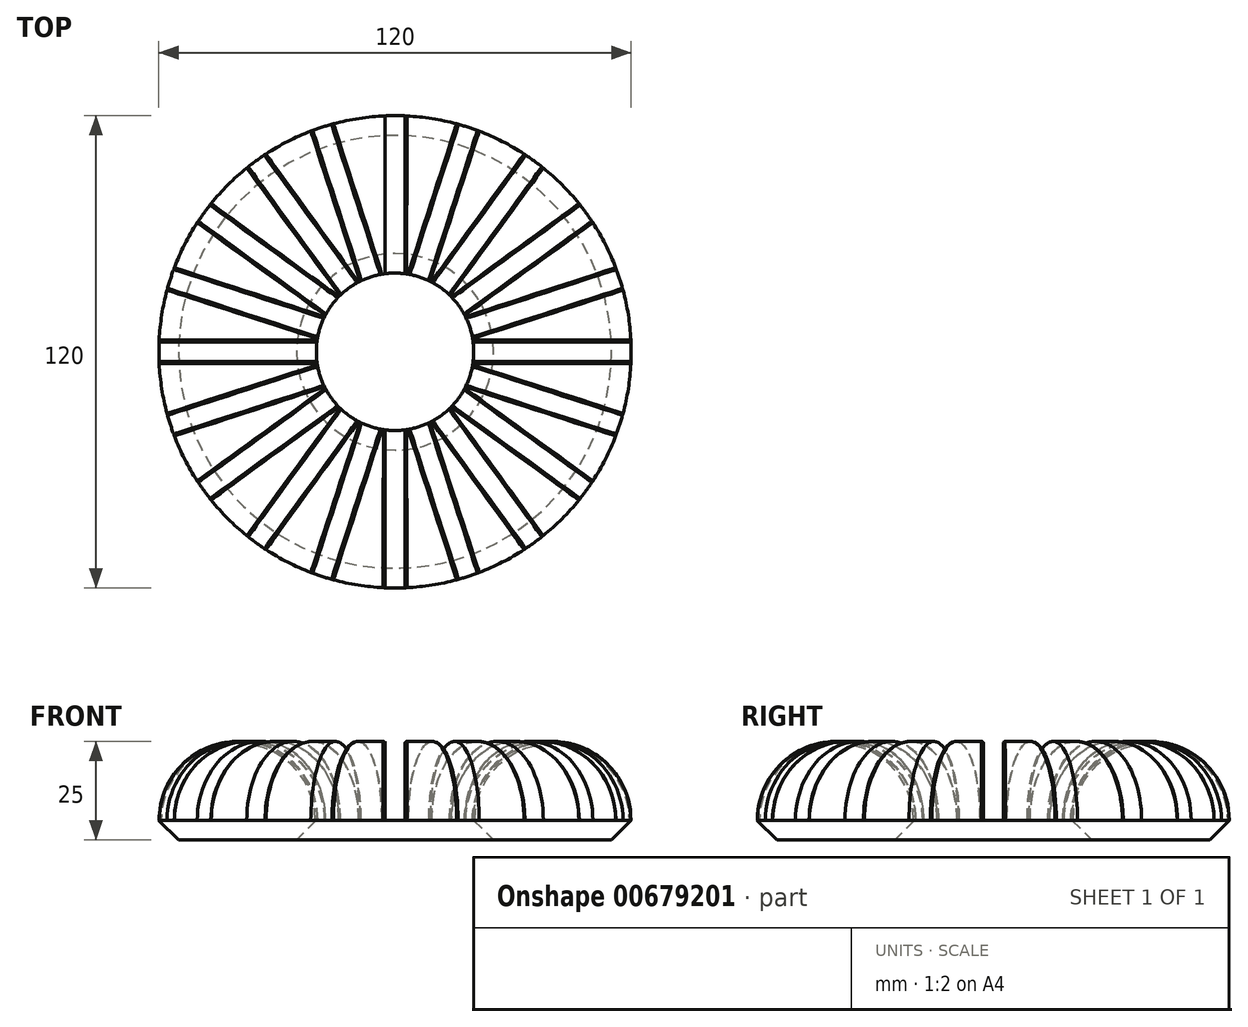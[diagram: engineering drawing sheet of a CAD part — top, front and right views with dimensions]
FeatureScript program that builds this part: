
annotation { "Feature Type Name" : "Feature", "Feature Type Description" : "" }
export const myFeature = defineFeature(function(context is Context, id is Id, definition is map)
    precondition{}
    {
        {
            var Q0;
            Q0=qCreatedBy(makeId("Front.planeOp"),FACE);
            var sketch = newSketch(context, id + "F0", { "sketchPlane" : qUnion([Q0])});
            skCircle(sketch, "E0", {"center": v(-40, 0) * mm, "radius": 20 * mm});
            skLineSegment(sketch, "E1", {"start": v(0, 10.53) * mm, "end": v(0, -11.09) * mm, "construction": true});
            skSolve(sketch);
        }
        {
            var Q0;
            Q0=makeQuery(id+"F0.imprint","IMPRINT",FACE,{"disambiguationData":[TD([[makeQuery(id+"F0.imprint","IMPRINT",EDGE,{"derivedFrom":sQuery(id+"F0.wireOp",EDGE,"E0")}),1.0]])]});
            var Q1;
            Q1=sQuery(id+"F0.wireOp",EDGE,"E1");
            revolve(context, id + "F1", {"entities" : qUnion([Q0]), "axis" : qUnion([Q1]), "revolveType" : RevolveType.FULL});
        }
        {
            var Q0;
            Q0=qCreatedBy(makeId("Top.planeOp"),FACE);
            var sketch = newSketch(context, id + "F2", { "sketchPlane" : qUnion([Q0])});
            skLineSegment(sketch, "E2.bottom", {"start": v(-120, 2.5) * mm, "end": v(0, 2.5) * mm});
            skLineSegment(sketch, "E2.top", {"start": v(-120, -2.5) * mm, "end": v(0, -2.5) * mm});
            skLineSegment(sketch, "E2.left", {"start": v(-120, 2.5) * mm, "end": v(-120, -2.5) * mm});
            skLineSegment(sketch, "E2.right", {"start": v(0, 2.5) * mm, "end": v(0, -2.5) * mm});
            skSolve(sketch);
        }
        {
            var Q0;
            Q0=makeQuery(id+"F2.imprint","IMPRINT",FACE,{"disambiguationData":[TD([[makeQuery(id+"F2.imprint","IMPRINT",EDGE,{"derivedFrom":sQuery(id+"F2.wireOp",EDGE,"E2.bottom")}),-1.0]])]});
            extrude(context, id + "F3", {"entities" : qUnion([Q0]), "depth" : 25 * mm, "offsetDistance" : 25 * mm});
        }
        {
            var Q0;
            Q0=makeQuery(id+"F3.opExtrude","SWEPT_BODY",BODY,{"disambiguationData":[OSD([sQuery(id+"F2.wireOp",EDGE,"E2.bottom"),sQuery(id+"F2.wireOp",EDGE,"E2.top"),sQuery(id+"F2.wireOp",EDGE,"E2.left"),sQuery(id+"F2.wireOp",EDGE,"E2.right")])]});
            var Q1;
            Q1=makeQuery(id+"F1.opRevolve","SWEPT_FACE",FACE,{"disambiguationData":[OSD([sQuery(id+"F0.wireOp",EDGE,"E0")])]});
            circularPattern(context, id + "F4", {"operationType" : NewBodyOperationType.REMOVE, "entities" : qUnion([Q0]), "axis" : qUnion([Q1]), "angle" : 360 * degree, "instanceCount" : 20, "equalSpace" : true});
        }
        {
            var Q0;
            Q0=qCreatedBy(makeId("Right.planeOp"),FACE);
            var sketch = newSketch(context, id + "F5", { "sketchPlane" : qUnion([Q0])});
            skLineSegment(sketch, "E3.bottom", {"start": v(-64.64, -5) * mm, "end": v(73.85, -5) * mm});
            skLineSegment(sketch, "E3.top", {"start": v(-64.64, -32.55) * mm, "end": v(73.85, -32.55) * mm});
            skLineSegment(sketch, "E3.left", {"start": v(-64.64, -5) * mm, "end": v(-64.64, -32.55) * mm});
            skLineSegment(sketch, "E3.right", {"start": v(73.85, -5) * mm, "end": v(73.85, -32.55) * mm});
            skSolve(sketch);
        }
        {
            var Q0;
            Q0=makeQuery(id+"F5.imprint","IMPRINT",FACE,{"disambiguationData":[TD([[makeQuery(id+"F5.imprint","IMPRINT",EDGE,{"derivedFrom":sQuery(id+"F5.wireOp",EDGE,"E3.bottom")}),-1.0]])]});
            extrude(context, id + "F6", {"entities" : qUnion([Q0]), "operationType" : NewBodyOperationType.REMOVE, "endBound" : BoundingType.SYMMETRIC, "oppositeDirection" : true, "depth" : 180 * mm, "offsetDistance" : 25 * mm});
        }
        {
            var Q0;
            Q0=makeQuery(id+"F6.boolean.opBoolean","INTERSECT",EDGE,{"disambiguationData":[OD(0.0)],"derivedFrom":[makeQuery(id+"F1.opRevolve","SWEPT_FACE",FACE,{"disambiguationData":[OSD([sQuery(id+"F0.wireOp",EDGE,"E0")])]}),makeQuery(id+"F6.opExtrude","SWEPT_FACE",FACE,{"disambiguationData":[OSD([sQuery(id+"F5.wireOp",EDGE,"E3.bottom")])]})]});
            var Q1;
            Q1=makeQuery(id+"F6.boolean.opBoolean","INTERSECT",EDGE,{"disambiguationData":[OD(1.0)],"derivedFrom":[makeQuery(id+"F1.opRevolve","SWEPT_FACE",FACE,{"disambiguationData":[OSD([sQuery(id+"F0.wireOp",EDGE,"E0")])]}),makeQuery(id+"F6.opExtrude","SWEPT_FACE",FACE,{"disambiguationData":[OSD([sQuery(id+"F5.wireOp",EDGE,"E3.bottom")])]})]});
            chamfer(context, id + "F7", {"entities" : qUnion([Q0, Q1]), "width" : 5 * mm, "tangentPropagation" : true});
        }
        {
            var Q0;
            Q0=makeQuery(id+"F4.boolean.opBoolean","INTERSECT",EDGE,{"derivedFrom":[makeQuery(id+"F1.opRevolve","SWEPT_FACE",FACE,{"disambiguationData":[OSD([sQuery(id+"F0.wireOp",EDGE,"E0")])]}),makeQuery(id+"F4.opPattern","COPY",FACE,{"derivedFrom":makeQuery(id+"F3.opExtrude","SWEPT_FACE",FACE,{"disambiguationData":[OSD([sQuery(id+"F2.wireOp",EDGE,"E2.bottom")])]}),"instanceName":"4"})]});
            var Q1;
            Q1=makeQuery(id+"F4.boolean.opBoolean","INTERSECT",EDGE,{"derivedFrom":[makeQuery(id+"F1.opRevolve","SWEPT_FACE",FACE,{"disambiguationData":[OSD([sQuery(id+"F0.wireOp",EDGE,"E0")])]}),makeQuery(id+"F4.opPattern","COPY",FACE,{"derivedFrom":makeQuery(id+"F3.opExtrude","SWEPT_FACE",FACE,{"disambiguationData":[OSD([sQuery(id+"F2.wireOp",EDGE,"E2.top")])]}),"instanceName":"3"})]});
            var Q2;
            Q2=makeQuery(id+"F4.boolean.opBoolean","INTERSECT",EDGE,{"derivedFrom":[makeQuery(id+"F1.opRevolve","SWEPT_FACE",FACE,{"disambiguationData":[OSD([sQuery(id+"F0.wireOp",EDGE,"E0")])]}),makeQuery(id+"F4.opPattern","COPY",FACE,{"derivedFrom":makeQuery(id+"F3.opExtrude","SWEPT_FACE",FACE,{"disambiguationData":[OSD([sQuery(id+"F2.wireOp",EDGE,"E2.bottom")])]}),"instanceName":"3"})]});
            var Q3;
            Q3=makeQuery(id+"F4.boolean.opBoolean","INTERSECT",EDGE,{"derivedFrom":[makeQuery(id+"F1.opRevolve","SWEPT_FACE",FACE,{"disambiguationData":[OSD([sQuery(id+"F0.wireOp",EDGE,"E0")])]}),makeQuery(id+"F4.opPattern","COPY",FACE,{"derivedFrom":makeQuery(id+"F3.opExtrude","SWEPT_FACE",FACE,{"disambiguationData":[OSD([sQuery(id+"F2.wireOp",EDGE,"E2.top")])]}),"instanceName":"2"})]});
            var Q4;
            Q4=makeQuery(id+"F4.boolean.opBoolean","INTERSECT",EDGE,{"derivedFrom":[makeQuery(id+"F1.opRevolve","SWEPT_FACE",FACE,{"disambiguationData":[OSD([sQuery(id+"F0.wireOp",EDGE,"E0")])]}),makeQuery(id+"F4.opPattern","COPY",FACE,{"derivedFrom":makeQuery(id+"F3.opExtrude","SWEPT_FACE",FACE,{"disambiguationData":[OSD([sQuery(id+"F2.wireOp",EDGE,"E2.bottom")])]}),"instanceName":"2"})]});
            var Q5;
            Q5=makeQuery(id+"F4.boolean.opBoolean","INTERSECT",EDGE,{"derivedFrom":[makeQuery(id+"F1.opRevolve","SWEPT_FACE",FACE,{"disambiguationData":[OSD([sQuery(id+"F0.wireOp",EDGE,"E0")])]}),makeQuery(id+"F4.opPattern","COPY",FACE,{"derivedFrom":makeQuery(id+"F3.opExtrude","SWEPT_FACE",FACE,{"disambiguationData":[OSD([sQuery(id+"F2.wireOp",EDGE,"E2.top")])]}),"instanceName":"1"})]});
            var Q6;
            Q6=makeQuery(id+"F4.boolean.opBoolean","INTERSECT",EDGE,{"derivedFrom":[makeQuery(id+"F1.opRevolve","SWEPT_FACE",FACE,{"disambiguationData":[OSD([sQuery(id+"F0.wireOp",EDGE,"E0")])]}),makeQuery(id+"F4.opPattern","COPY",FACE,{"derivedFrom":makeQuery(id+"F3.opExtrude","SWEPT_FACE",FACE,{"disambiguationData":[OSD([sQuery(id+"F2.wireOp",EDGE,"E2.bottom")])]}),"instanceName":"1"})]});
            var Q7;
            Q7=makeQuery(id+"F4.boolean.opBoolean","INTERSECT",EDGE,{"derivedFrom":[makeQuery(id+"F1.opRevolve","SWEPT_FACE",FACE,{"disambiguationData":[OSD([sQuery(id+"F0.wireOp",EDGE,"E0")])]}),makeQuery(id+"F3.opExtrude","SWEPT_FACE",FACE,{"disambiguationData":[OSD([sQuery(id+"F2.wireOp",EDGE,"E2.top")])]})]});
            var Q8;
            Q8=makeQuery(id+"F4.boolean.opBoolean","INTERSECT",EDGE,{"derivedFrom":[makeQuery(id+"F1.opRevolve","SWEPT_FACE",FACE,{"disambiguationData":[OSD([sQuery(id+"F0.wireOp",EDGE,"E0")])]}),makeQuery(id+"F3.opExtrude","SWEPT_FACE",FACE,{"disambiguationData":[OSD([sQuery(id+"F2.wireOp",EDGE,"E2.bottom")])]})]});
            var Q9;
            Q9=makeQuery(id+"F4.boolean.opBoolean","INTERSECT",EDGE,{"derivedFrom":[makeQuery(id+"F1.opRevolve","SWEPT_FACE",FACE,{"disambiguationData":[OSD([sQuery(id+"F0.wireOp",EDGE,"E0")])]}),makeQuery(id+"F4.opPattern","COPY",FACE,{"derivedFrom":makeQuery(id+"F3.opExtrude","SWEPT_FACE",FACE,{"disambiguationData":[OSD([sQuery(id+"F2.wireOp",EDGE,"E2.top")])]}),"instanceName":"19"})]});
            var Q10;
            Q10=makeQuery(id+"F4.boolean.opBoolean","INTERSECT",EDGE,{"derivedFrom":[makeQuery(id+"F1.opRevolve","SWEPT_FACE",FACE,{"disambiguationData":[OSD([sQuery(id+"F0.wireOp",EDGE,"E0")])]}),makeQuery(id+"F4.opPattern","COPY",FACE,{"derivedFrom":makeQuery(id+"F3.opExtrude","SWEPT_FACE",FACE,{"disambiguationData":[OSD([sQuery(id+"F2.wireOp",EDGE,"E2.bottom")])]}),"instanceName":"19"})]});
            var Q11;
            Q11=makeQuery(id+"F4.boolean.opBoolean","INTERSECT",EDGE,{"derivedFrom":[makeQuery(id+"F1.opRevolve","SWEPT_FACE",FACE,{"disambiguationData":[OSD([sQuery(id+"F0.wireOp",EDGE,"E0")])]}),makeQuery(id+"F4.opPattern","COPY",FACE,{"derivedFrom":makeQuery(id+"F3.opExtrude","SWEPT_FACE",FACE,{"disambiguationData":[OSD([sQuery(id+"F2.wireOp",EDGE,"E2.top")])]}),"instanceName":"18"})]});
            var Q12;
            Q12=makeQuery(id+"F4.boolean.opBoolean","INTERSECT",EDGE,{"derivedFrom":[makeQuery(id+"F1.opRevolve","SWEPT_FACE",FACE,{"disambiguationData":[OSD([sQuery(id+"F0.wireOp",EDGE,"E0")])]}),makeQuery(id+"F4.opPattern","COPY",FACE,{"derivedFrom":makeQuery(id+"F3.opExtrude","SWEPT_FACE",FACE,{"disambiguationData":[OSD([sQuery(id+"F2.wireOp",EDGE,"E2.bottom")])]}),"instanceName":"18"})]});
            var Q13;
            Q13=makeQuery(id+"F4.boolean.opBoolean","INTERSECT",EDGE,{"derivedFrom":[makeQuery(id+"F1.opRevolve","SWEPT_FACE",FACE,{"disambiguationData":[OSD([sQuery(id+"F0.wireOp",EDGE,"E0")])]}),makeQuery(id+"F4.opPattern","COPY",FACE,{"derivedFrom":makeQuery(id+"F3.opExtrude","SWEPT_FACE",FACE,{"disambiguationData":[OSD([sQuery(id+"F2.wireOp",EDGE,"E2.top")])]}),"instanceName":"17"})]});
            var Q14;
            Q14=makeQuery(id+"F4.boolean.opBoolean","INTERSECT",EDGE,{"derivedFrom":[makeQuery(id+"F1.opRevolve","SWEPT_FACE",FACE,{"disambiguationData":[OSD([sQuery(id+"F0.wireOp",EDGE,"E0")])]}),makeQuery(id+"F4.opPattern","COPY",FACE,{"derivedFrom":makeQuery(id+"F3.opExtrude","SWEPT_FACE",FACE,{"disambiguationData":[OSD([sQuery(id+"F2.wireOp",EDGE,"E2.bottom")])]}),"instanceName":"17"})]});
            var Q15;
            Q15=makeQuery(id+"F4.boolean.opBoolean","INTERSECT",EDGE,{"derivedFrom":[makeQuery(id+"F1.opRevolve","SWEPT_FACE",FACE,{"disambiguationData":[OSD([sQuery(id+"F0.wireOp",EDGE,"E0")])]}),makeQuery(id+"F4.opPattern","COPY",FACE,{"derivedFrom":makeQuery(id+"F3.opExtrude","SWEPT_FACE",FACE,{"disambiguationData":[OSD([sQuery(id+"F2.wireOp",EDGE,"E2.top")])]}),"instanceName":"16"})]});
            var Q16;
            Q16=makeQuery(id+"F4.boolean.opBoolean","INTERSECT",EDGE,{"derivedFrom":[makeQuery(id+"F1.opRevolve","SWEPT_FACE",FACE,{"disambiguationData":[OSD([sQuery(id+"F0.wireOp",EDGE,"E0")])]}),makeQuery(id+"F4.opPattern","COPY",FACE,{"derivedFrom":makeQuery(id+"F3.opExtrude","SWEPT_FACE",FACE,{"disambiguationData":[OSD([sQuery(id+"F2.wireOp",EDGE,"E2.bottom")])]}),"instanceName":"16"})]});
            var Q17;
            Q17=makeQuery(id+"F4.boolean.opBoolean","INTERSECT",EDGE,{"derivedFrom":[makeQuery(id+"F1.opRevolve","SWEPT_FACE",FACE,{"disambiguationData":[OSD([sQuery(id+"F0.wireOp",EDGE,"E0")])]}),makeQuery(id+"F4.opPattern","COPY",FACE,{"derivedFrom":makeQuery(id+"F3.opExtrude","SWEPT_FACE",FACE,{"disambiguationData":[OSD([sQuery(id+"F2.wireOp",EDGE,"E2.bottom")])]}),"instanceName":"15"})]});
            var Q18;
            Q18=makeQuery(id+"F4.boolean.opBoolean","INTERSECT",EDGE,{"derivedFrom":[makeQuery(id+"F1.opRevolve","SWEPT_FACE",FACE,{"disambiguationData":[OSD([sQuery(id+"F0.wireOp",EDGE,"E0")])]}),makeQuery(id+"F4.opPattern","COPY",FACE,{"derivedFrom":makeQuery(id+"F3.opExtrude","SWEPT_FACE",FACE,{"disambiguationData":[OSD([sQuery(id+"F2.wireOp",EDGE,"E2.top")])]}),"instanceName":"14"})]});
            var Q19;
            Q19=makeQuery(id+"F4.boolean.opBoolean","INTERSECT",EDGE,{"derivedFrom":[makeQuery(id+"F1.opRevolve","SWEPT_FACE",FACE,{"disambiguationData":[OSD([sQuery(id+"F0.wireOp",EDGE,"E0")])]}),makeQuery(id+"F4.opPattern","COPY",FACE,{"derivedFrom":makeQuery(id+"F3.opExtrude","SWEPT_FACE",FACE,{"disambiguationData":[OSD([sQuery(id+"F2.wireOp",EDGE,"E2.bottom")])]}),"instanceName":"14"})]});
            var Q20;
            Q20=makeQuery(id+"F4.boolean.opBoolean","INTERSECT",EDGE,{"derivedFrom":[makeQuery(id+"F1.opRevolve","SWEPT_FACE",FACE,{"disambiguationData":[OSD([sQuery(id+"F0.wireOp",EDGE,"E0")])]}),makeQuery(id+"F4.opPattern","COPY",FACE,{"derivedFrom":makeQuery(id+"F3.opExtrude","SWEPT_FACE",FACE,{"disambiguationData":[OSD([sQuery(id+"F2.wireOp",EDGE,"E2.top")])]}),"instanceName":"13"})]});
            var Q21;
            Q21=makeQuery(id+"F4.boolean.opBoolean","INTERSECT",EDGE,{"derivedFrom":[makeQuery(id+"F1.opRevolve","SWEPT_FACE",FACE,{"disambiguationData":[OSD([sQuery(id+"F0.wireOp",EDGE,"E0")])]}),makeQuery(id+"F4.opPattern","COPY",FACE,{"derivedFrom":makeQuery(id+"F3.opExtrude","SWEPT_FACE",FACE,{"disambiguationData":[OSD([sQuery(id+"F2.wireOp",EDGE,"E2.bottom")])]}),"instanceName":"13"})]});
            var Q22;
            Q22=makeQuery(id+"F4.boolean.opBoolean","INTERSECT",EDGE,{"derivedFrom":[makeQuery(id+"F1.opRevolve","SWEPT_FACE",FACE,{"disambiguationData":[OSD([sQuery(id+"F0.wireOp",EDGE,"E0")])]}),makeQuery(id+"F4.opPattern","COPY",FACE,{"derivedFrom":makeQuery(id+"F3.opExtrude","SWEPT_FACE",FACE,{"disambiguationData":[OSD([sQuery(id+"F2.wireOp",EDGE,"E2.bottom")])]}),"instanceName":"12"})]});
            var Q23;
            Q23=makeQuery(id+"F4.boolean.opBoolean","INTERSECT",EDGE,{"derivedFrom":[makeQuery(id+"F1.opRevolve","SWEPT_FACE",FACE,{"disambiguationData":[OSD([sQuery(id+"F0.wireOp",EDGE,"E0")])]}),makeQuery(id+"F4.opPattern","COPY",FACE,{"derivedFrom":makeQuery(id+"F3.opExtrude","SWEPT_FACE",FACE,{"disambiguationData":[OSD([sQuery(id+"F2.wireOp",EDGE,"E2.top")])]}),"instanceName":"11"})]});
            var Q24;
            Q24=makeQuery(id+"F4.boolean.opBoolean","INTERSECT",EDGE,{"derivedFrom":[makeQuery(id+"F1.opRevolve","SWEPT_FACE",FACE,{"disambiguationData":[OSD([sQuery(id+"F0.wireOp",EDGE,"E0")])]}),makeQuery(id+"F4.opPattern","COPY",FACE,{"derivedFrom":makeQuery(id+"F3.opExtrude","SWEPT_FACE",FACE,{"disambiguationData":[OSD([sQuery(id+"F2.wireOp",EDGE,"E2.bottom")])]}),"instanceName":"11"})]});
            var Q25;
            Q25=makeQuery(id+"F4.boolean.opBoolean","INTERSECT",EDGE,{"derivedFrom":[makeQuery(id+"F1.opRevolve","SWEPT_FACE",FACE,{"disambiguationData":[OSD([sQuery(id+"F0.wireOp",EDGE,"E0")])]}),makeQuery(id+"F4.opPattern","COPY",FACE,{"derivedFrom":makeQuery(id+"F3.opExtrude","SWEPT_FACE",FACE,{"disambiguationData":[OSD([sQuery(id+"F2.wireOp",EDGE,"E2.top")])]}),"instanceName":"10"})]});
            var Q26;
            Q26=makeQuery(id+"F4.boolean.opBoolean","INTERSECT",EDGE,{"derivedFrom":[makeQuery(id+"F1.opRevolve","SWEPT_FACE",FACE,{"disambiguationData":[OSD([sQuery(id+"F0.wireOp",EDGE,"E0")])]}),makeQuery(id+"F4.opPattern","COPY",FACE,{"derivedFrom":makeQuery(id+"F3.opExtrude","SWEPT_FACE",FACE,{"disambiguationData":[OSD([sQuery(id+"F2.wireOp",EDGE,"E2.bottom")])]}),"instanceName":"10"})]});
            var Q27;
            Q27=makeQuery(id+"F4.boolean.opBoolean","INTERSECT",EDGE,{"derivedFrom":[makeQuery(id+"F1.opRevolve","SWEPT_FACE",FACE,{"disambiguationData":[OSD([sQuery(id+"F0.wireOp",EDGE,"E0")])]}),makeQuery(id+"F4.opPattern","COPY",FACE,{"derivedFrom":makeQuery(id+"F3.opExtrude","SWEPT_FACE",FACE,{"disambiguationData":[OSD([sQuery(id+"F2.wireOp",EDGE,"E2.top")])]}),"instanceName":"9"})]});
            var Q28;
            Q28=makeQuery(id+"F4.boolean.opBoolean","INTERSECT",EDGE,{"derivedFrom":[makeQuery(id+"F1.opRevolve","SWEPT_FACE",FACE,{"disambiguationData":[OSD([sQuery(id+"F0.wireOp",EDGE,"E0")])]}),makeQuery(id+"F4.opPattern","COPY",FACE,{"derivedFrom":makeQuery(id+"F3.opExtrude","SWEPT_FACE",FACE,{"disambiguationData":[OSD([sQuery(id+"F2.wireOp",EDGE,"E2.top")])]}),"instanceName":"12"})]});
            var Q29;
            Q29=makeQuery(id+"F4.boolean.opBoolean","INTERSECT",EDGE,{"derivedFrom":[makeQuery(id+"F1.opRevolve","SWEPT_FACE",FACE,{"disambiguationData":[OSD([sQuery(id+"F0.wireOp",EDGE,"E0")])]}),makeQuery(id+"F4.opPattern","COPY",FACE,{"derivedFrom":makeQuery(id+"F3.opExtrude","SWEPT_FACE",FACE,{"disambiguationData":[OSD([sQuery(id+"F2.wireOp",EDGE,"E2.bottom")])]}),"instanceName":"9"})]});
            var Q30;
            Q30=makeQuery(id+"F4.boolean.opBoolean","INTERSECT",EDGE,{"derivedFrom":[makeQuery(id+"F1.opRevolve","SWEPT_FACE",FACE,{"disambiguationData":[OSD([sQuery(id+"F0.wireOp",EDGE,"E0")])]}),makeQuery(id+"F4.opPattern","COPY",FACE,{"derivedFrom":makeQuery(id+"F3.opExtrude","SWEPT_FACE",FACE,{"disambiguationData":[OSD([sQuery(id+"F2.wireOp",EDGE,"E2.top")])]}),"instanceName":"8"})]});
            var Q31;
            Q31=makeQuery(id+"F4.boolean.opBoolean","INTERSECT",EDGE,{"derivedFrom":[makeQuery(id+"F1.opRevolve","SWEPT_FACE",FACE,{"disambiguationData":[OSD([sQuery(id+"F0.wireOp",EDGE,"E0")])]}),makeQuery(id+"F4.opPattern","COPY",FACE,{"derivedFrom":makeQuery(id+"F3.opExtrude","SWEPT_FACE",FACE,{"disambiguationData":[OSD([sQuery(id+"F2.wireOp",EDGE,"E2.bottom")])]}),"instanceName":"8"})]});
            var Q32;
            Q32=makeQuery(id+"F4.boolean.opBoolean","INTERSECT",EDGE,{"derivedFrom":[makeQuery(id+"F1.opRevolve","SWEPT_FACE",FACE,{"disambiguationData":[OSD([sQuery(id+"F0.wireOp",EDGE,"E0")])]}),makeQuery(id+"F4.opPattern","COPY",FACE,{"derivedFrom":makeQuery(id+"F3.opExtrude","SWEPT_FACE",FACE,{"disambiguationData":[OSD([sQuery(id+"F2.wireOp",EDGE,"E2.top")])]}),"instanceName":"7"})]});
            var Q33;
            Q33=makeQuery(id+"F4.boolean.opBoolean","INTERSECT",EDGE,{"derivedFrom":[makeQuery(id+"F1.opRevolve","SWEPT_FACE",FACE,{"disambiguationData":[OSD([sQuery(id+"F0.wireOp",EDGE,"E0")])]}),makeQuery(id+"F4.opPattern","COPY",FACE,{"derivedFrom":makeQuery(id+"F3.opExtrude","SWEPT_FACE",FACE,{"disambiguationData":[OSD([sQuery(id+"F2.wireOp",EDGE,"E2.bottom")])]}),"instanceName":"7"})]});
            var Q34;
            Q34=makeQuery(id+"F4.boolean.opBoolean","INTERSECT",EDGE,{"derivedFrom":[makeQuery(id+"F1.opRevolve","SWEPT_FACE",FACE,{"disambiguationData":[OSD([sQuery(id+"F0.wireOp",EDGE,"E0")])]}),makeQuery(id+"F4.opPattern","COPY",FACE,{"derivedFrom":makeQuery(id+"F3.opExtrude","SWEPT_FACE",FACE,{"disambiguationData":[OSD([sQuery(id+"F2.wireOp",EDGE,"E2.top")])]}),"instanceName":"6"})]});
            var Q35;
            Q35=makeQuery(id+"F4.boolean.opBoolean","INTERSECT",EDGE,{"derivedFrom":[makeQuery(id+"F1.opRevolve","SWEPT_FACE",FACE,{"disambiguationData":[OSD([sQuery(id+"F0.wireOp",EDGE,"E0")])]}),makeQuery(id+"F4.opPattern","COPY",FACE,{"derivedFrom":makeQuery(id+"F3.opExtrude","SWEPT_FACE",FACE,{"disambiguationData":[OSD([sQuery(id+"F2.wireOp",EDGE,"E2.bottom")])]}),"instanceName":"6"})]});
            var Q36;
            Q36=makeQuery(id+"F4.boolean.opBoolean","INTERSECT",EDGE,{"derivedFrom":[makeQuery(id+"F1.opRevolve","SWEPT_FACE",FACE,{"disambiguationData":[OSD([sQuery(id+"F0.wireOp",EDGE,"E0")])]}),makeQuery(id+"F4.opPattern","COPY",FACE,{"derivedFrom":makeQuery(id+"F3.opExtrude","SWEPT_FACE",FACE,{"disambiguationData":[OSD([sQuery(id+"F2.wireOp",EDGE,"E2.top")])]}),"instanceName":"5"})]});
            var Q37;
            Q37=makeQuery(id+"F4.boolean.opBoolean","INTERSECT",EDGE,{"derivedFrom":[makeQuery(id+"F1.opRevolve","SWEPT_FACE",FACE,{"disambiguationData":[OSD([sQuery(id+"F0.wireOp",EDGE,"E0")])]}),makeQuery(id+"F4.opPattern","COPY",FACE,{"derivedFrom":makeQuery(id+"F3.opExtrude","SWEPT_FACE",FACE,{"disambiguationData":[OSD([sQuery(id+"F2.wireOp",EDGE,"E2.bottom")])]}),"instanceName":"5"})]});
            var Q38;
            Q38=makeQuery(id+"F4.boolean.opBoolean","INTERSECT",EDGE,{"derivedFrom":[makeQuery(id+"F1.opRevolve","SWEPT_FACE",FACE,{"disambiguationData":[OSD([sQuery(id+"F0.wireOp",EDGE,"E0")])]}),makeQuery(id+"F4.opPattern","COPY",FACE,{"derivedFrom":makeQuery(id+"F3.opExtrude","SWEPT_FACE",FACE,{"disambiguationData":[OSD([sQuery(id+"F2.wireOp",EDGE,"E2.top")])]}),"instanceName":"4"})]});
            fillet(context, id + "F8", {"entities" : qUnion([Q0, Q1, Q2, Q3, Q4, Q5, Q6, Q7, Q8, Q9, Q10, Q11, Q12, Q13, Q14, Q15, Q16, Q17, Q18, Q19, Q20, Q21, Q22, Q23, Q24, Q25, Q26, Q27, Q28, Q29, Q30, Q31, Q32, Q33, Q34, Q35, Q36, Q37, Q38]), "radius" : .5 * mm, "tangentPropagation" : true, "allowEdgeOverflow" : false});
        }
    });
